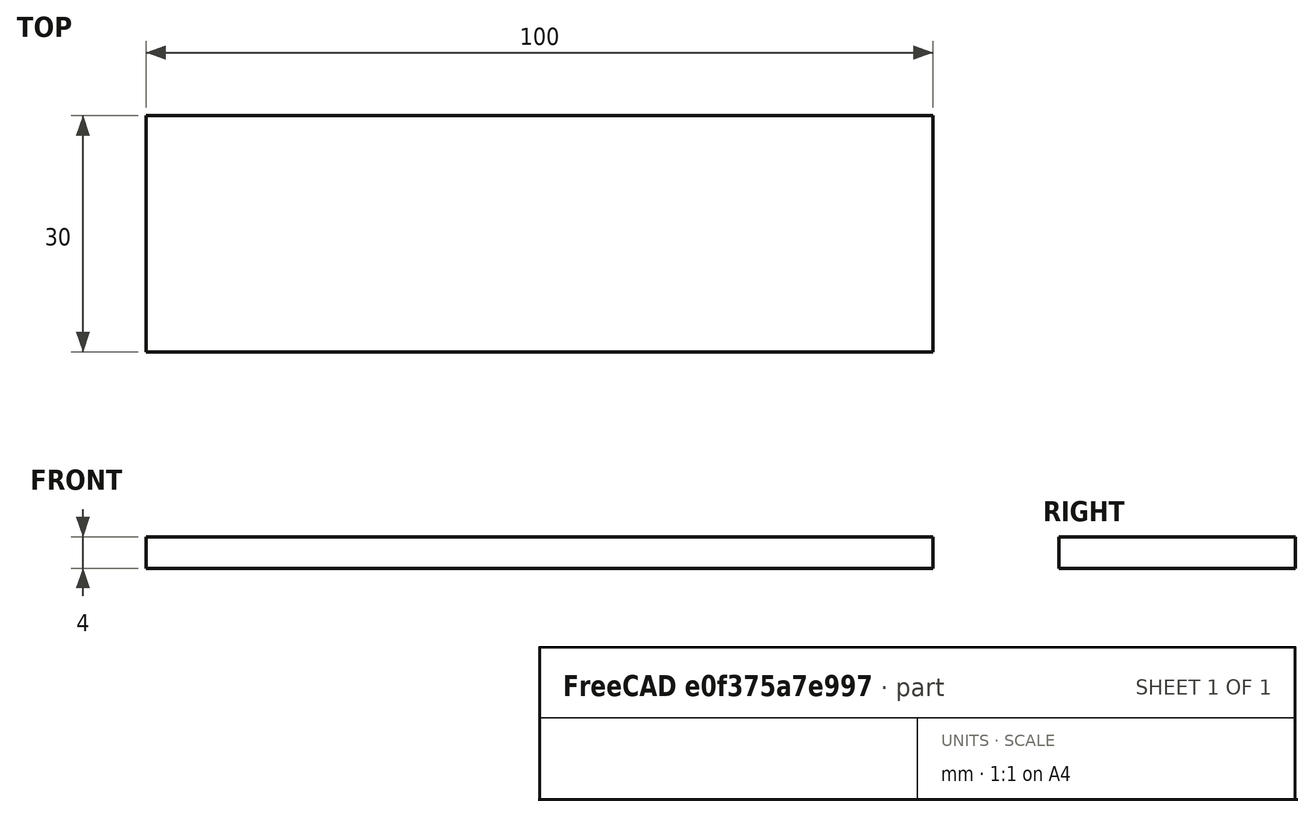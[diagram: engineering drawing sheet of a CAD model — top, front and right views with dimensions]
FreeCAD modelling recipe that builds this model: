
FCSTD DOCUMENT  (FreeCAD 0.16R6703 (Git))
Label: crater_border
License: Public Domain
LicenseURL: http://en.wikipedia.org/wiki/Public_domain
objects: Sketcher::SketchObject×1, PartDesign::Pad×1
note: 3 computed .brp shape members not serialized (recipe doc carries the construction recipe); baked Part::Feature solids carry a one-line shape summary decoded from their .brp

FEATURE [Sketcher::SketchObject] Sketch
  Placement = pos=(0,0,0) rot=(0.57735,0.57735,0.57735;2.0944rad)
  sketch-geometry (4):
    g0: LineSegment StartX=-12.8284 StartY=1.44635 StartZ=0 EndX=17.1716 EndY=1.44635 EndZ=0
    g1: LineSegment StartX=-12.8284 StartY=1.44635 StartZ=0 EndX=-12.8284 EndY=5.44635 EndZ=0
    g2: LineSegment StartX=-12.8284 StartY=5.44635 StartZ=0 EndX=17.1716 EndY=5.44635 EndZ=0
    g3: LineSegment StartX=17.1716 StartY=5.44635 StartZ=0 EndX=17.1716 EndY=1.44635 EndZ=0
  constraints (10):
    c: Horizontal(g0)
    c: DistanceX(g0,g0) = 30
    c: Coincident(g1,g0)
    c: Coincident(g2,g1)
    c: Coincident(g3,g2)
    c: Coincident(g3,g0)
    c: Horizontal(g2)
    c: Vertical(g3)
    c: Vertical(g1)
    c: DistanceY(g1,g1) = 4
FEATURE [PartDesign::Pad] Pad
  Length = 50
  Length2 = 50
  Placement = pos=(0,0,0) rot=(0.57735,0.57735,0.57735;2.0944rad)
  Sketch = -> Sketch
  Type = 4
